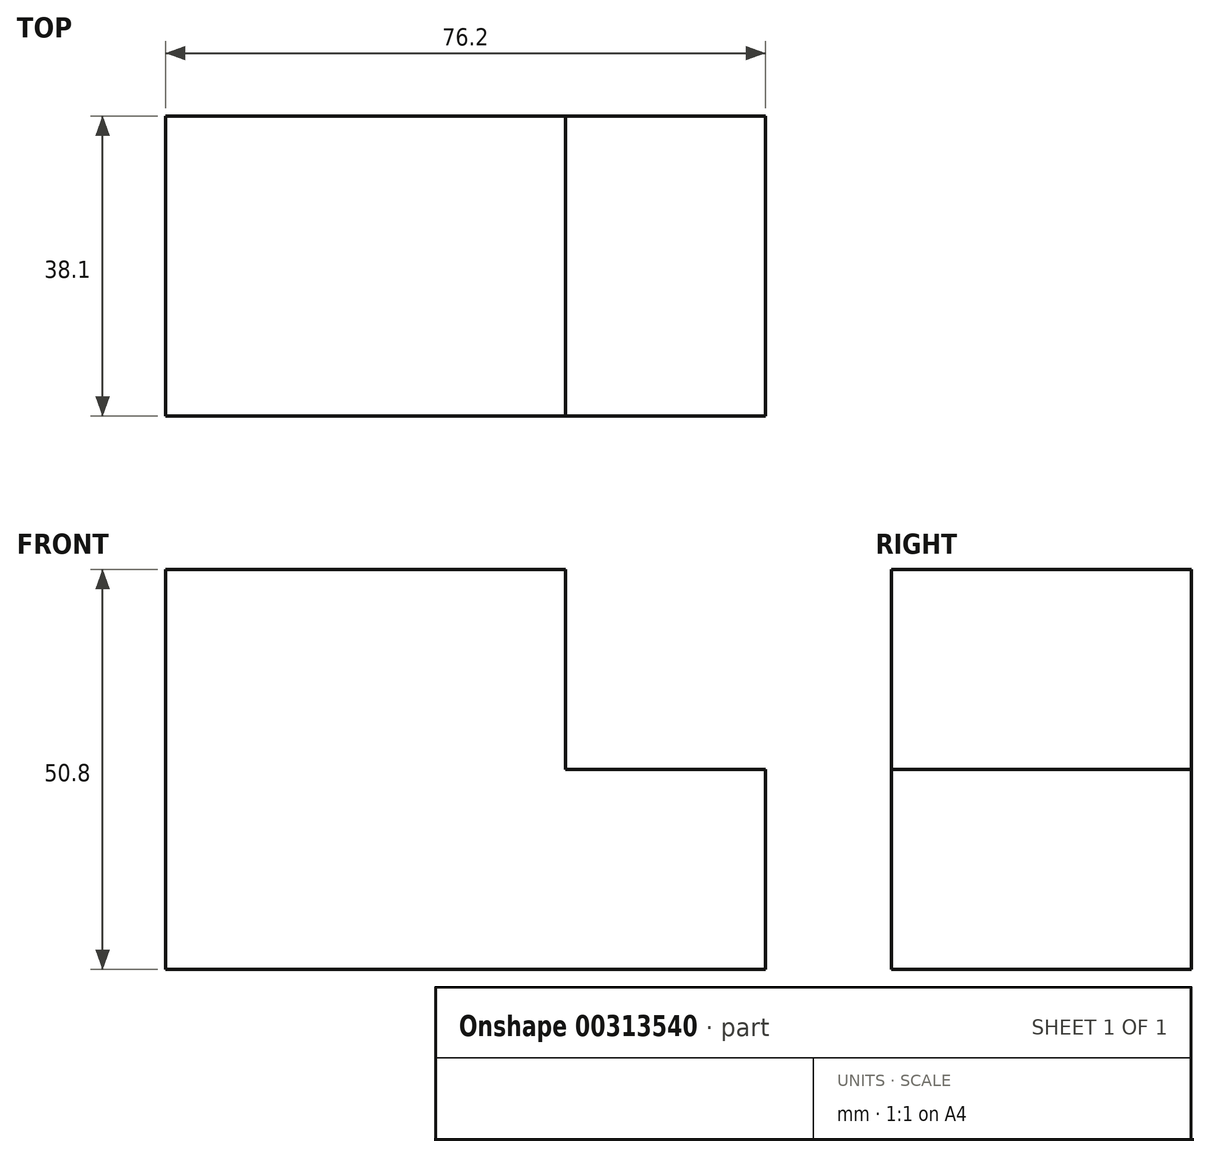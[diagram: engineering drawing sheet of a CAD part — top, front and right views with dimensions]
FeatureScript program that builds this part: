
annotation { "Feature Type Name" : "Feature", "Feature Type Description" : "" }
export const myFeature = defineFeature(function(context is Context, id is Id, definition is map)
    precondition{}
    {
        {
            var Q0;
            Q0=qCreatedBy(makeId("Front.planeOp"),FACE);
            var sketch = newSketch(context, id + "F0", { "sketchPlane" : qUnion([Q0])});
            skLineSegment(sketch, "E0", {"start": v(-40.54, -47.01) * mm, "end": v(35.66, -47.01) * mm});
            skLineSegment(sketch, "E1", {"start": v(35.66, -47.01) * mm, "end": v(35.66, -21.61) * mm});
            skLineSegment(sketch, "E2", {"start": v(35.66, -21.61) * mm, "end": v(10.26, -21.61) * mm});
            skLineSegment(sketch, "E3", {"start": v(10.26, -21.61) * mm, "end": v(10.26, 3.79) * mm});
            skLineSegment(sketch, "E4", {"start": v(10.26, 3.79) * mm, "end": v(-40.54, 3.79) * mm});
            skLineSegment(sketch, "E5", {"start": v(-40.54, 3.79) * mm, "end": v(-40.54, -47.01) * mm});
            skSolve(sketch);
        }
        {
            var Q0;
            Q0 = qSketchRegion(id + "F0", true);
            extrude(context, id + "F1", {"entities" : qUnion([Q0]), "depth" : 38.1 * mm});
        }
    });
